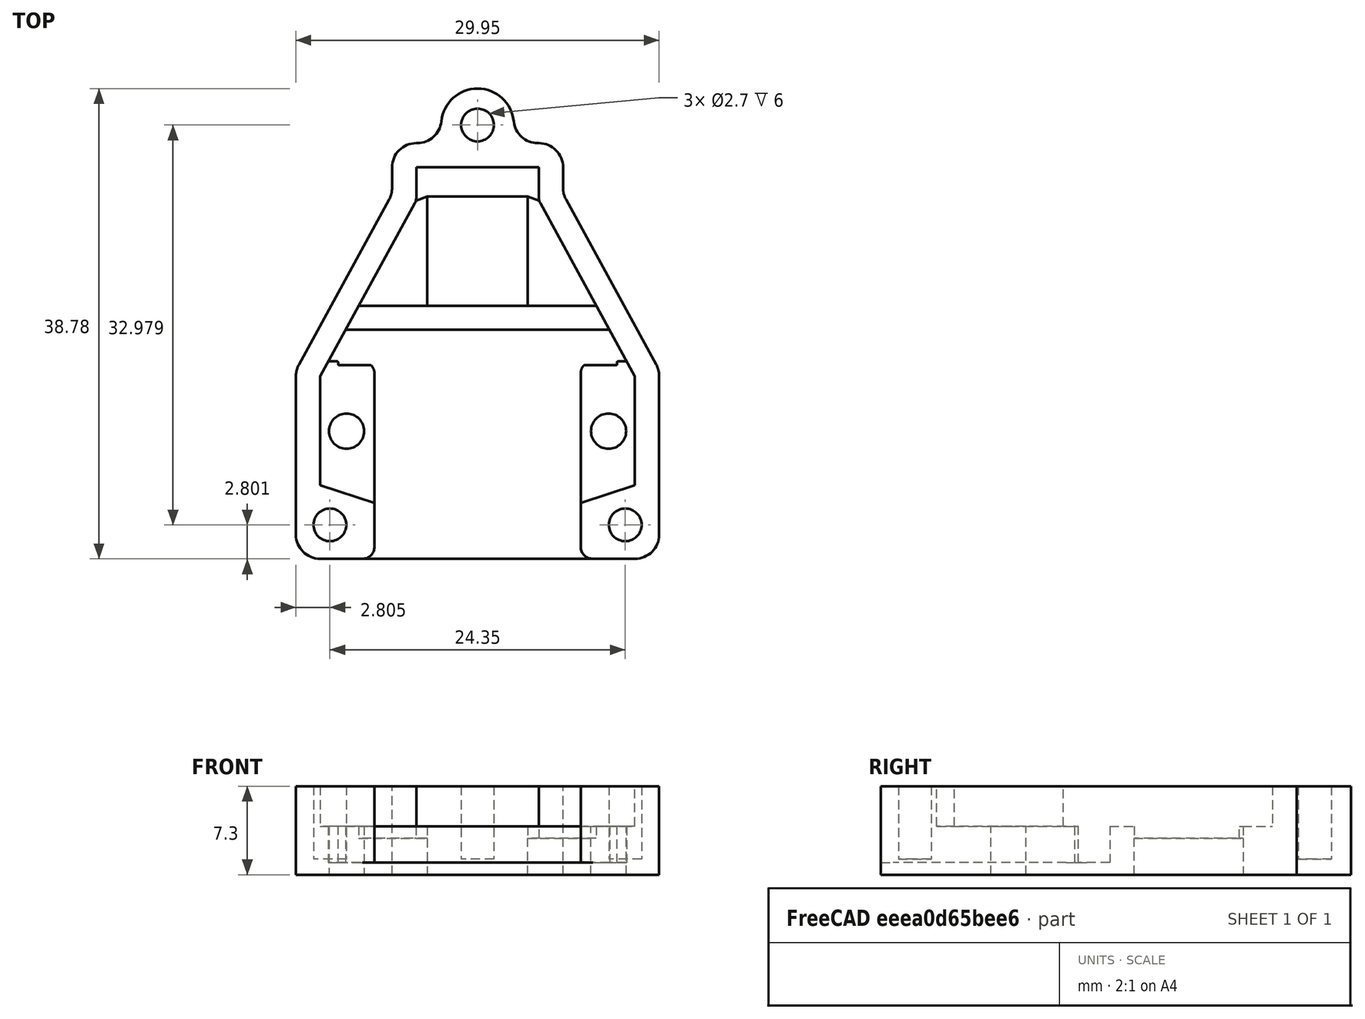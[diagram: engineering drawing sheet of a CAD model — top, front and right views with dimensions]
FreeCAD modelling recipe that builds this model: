
FCSTD DOCUMENT  (FreeCAD 0.14R3692 (Git))
Label: InkjetHolderHorizontalMount
License: CC-BY 3.0
LicenseURL: http://creativecommons.org/licenses/by/3.0/
objects: Part::Fillet×6, Part::Feature×1, Part::Box×1, Part::Cut×1
note: 9 computed .brp shape members not serialized (recipe doc carries the construction recipe); baked Part::Feature solids carry a one-line shape summary decoded from their .brp

FEATURE [Part::Feature] Part__Feature  label="InkjetHolderHorizontalMount1"
  shape: bbox 29.95 x 38.78 x 7.3 mm, 65 faces (baked)
FEATURE [Part::Box] Box  label="Cube"
  Height = 10
  Length = 23
  Placement = pos=(-11.5,9.7,-6) rot=(0,0,1;0rad)
  Width = 1
FEATURE [Part::Cut] Cut
  Base = -> Part__Feature
  Tool = -> Box
FEATURE [Part::Fillet] Fillet
  Base = -> Cut
  Edges = 1 edges r=0.07: [Edge162]
FEATURE [Part::Fillet] Fillet001
  Base = -> Fillet
  Edges = 1 edges r=0.07: [Edge25]
FEATURE [Part::Fillet] Fillet002
  Base = -> Fillet001
  Edges = 1 edges r=0.2: [Edge21]
FEATURE [Part::Fillet] Fillet003
  Base = -> Fillet002
  Edges = 1 edges r=0.07: [Edge196]
FEATURE [Part::Fillet] Fillet004
  Base = -> Fillet003
  Edges = 1 edges r=0.07: [Edge57]
FEATURE [Part::Fillet] Fillet005  label="InkjetHolderHorizontalMount"
  Base = -> Fillet004
  Edges = 1 edges r=0.2: [Edge15]
